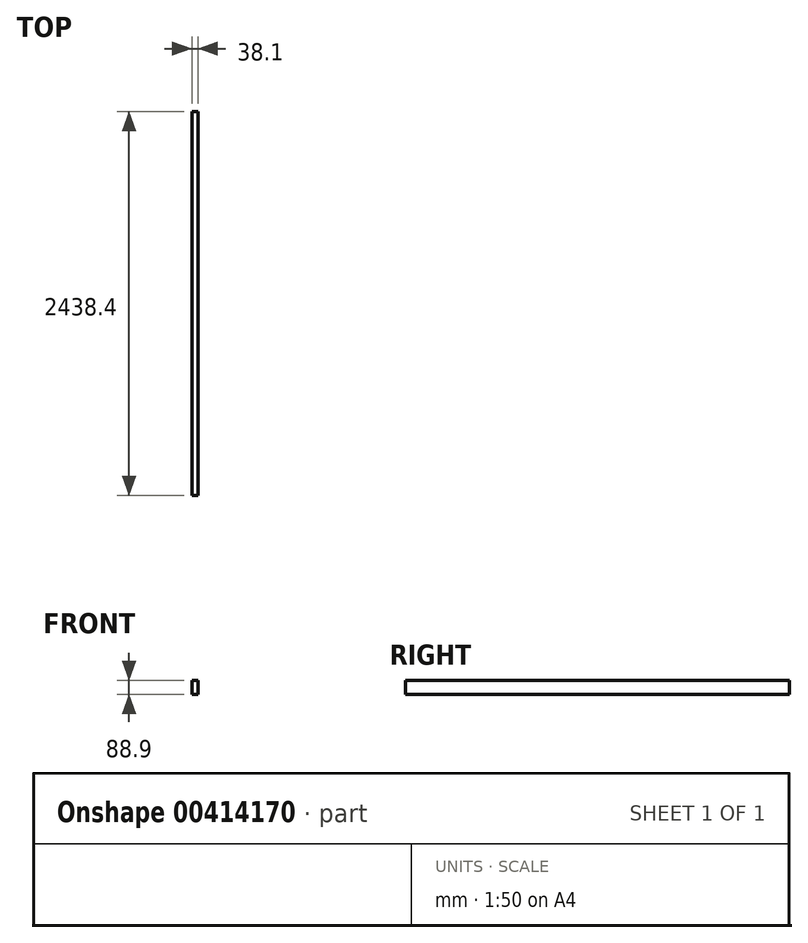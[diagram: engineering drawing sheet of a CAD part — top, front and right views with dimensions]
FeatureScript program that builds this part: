
annotation { "Feature Type Name" : "Feature", "Feature Type Description" : "" }
export const myFeature = defineFeature(function(context is Context, id is Id, definition is map)
    precondition{}
    {
        {
            var Q0;
            Q0=qCreatedBy(makeId("Front.planeOp"),FACE);
            var sketch = newSketch(context, id + "F0", { "sketchPlane" : qUnion([Q0])});
            skLineSegment(sketch, "E0.bottom", {"start": v(19.05, 44.45) * mm, "end": v(-19.05, 44.45) * mm});
            skLineSegment(sketch, "E0.top", {"start": v(19.05, -44.45) * mm, "end": v(-19.05, -44.45) * mm});
            skLineSegment(sketch, "E0.left", {"start": v(19.05, 44.45) * mm, "end": v(19.05, -44.45) * mm});
            skLineSegment(sketch, "E0.right", {"start": v(-19.05, 44.45) * mm, "end": v(-19.05, -44.45) * mm});
            skPoint(sketch, "E0.middle", {"position": v(0, 0) * mm});
            skSolve(sketch);
        }
        {
            var Q0;
            Q0 = qSketchRegion(id + "F0", true);
            extrude(context, id + "F1", {"entities" : qUnion([Q0]), "endBound" : BoundingType.SYMMETRIC, "depth" : 2438.4 * mm});
        }
    });
